FCSTD DOCUMENT  (FreeCAD 0.20R29603 (Git))
Label: wapama
License: All rights reserved
LicenseURL: http://en.wikipedia.org/wiki/All_rights_reserved
objects: Part::Vertex×236
note: 236 computed .brp shape members not serialized (recipe doc carries the construction recipe); baked Part::Feature solids carry a one-line shape summary decoded from their .brp

FEATURE [Part::Vertex] p1002  label="Sta-9_1/2-wl-13s"
  AttacherType = Attacher::AttachEngine3D
  X = 2498.72
  Y = 59966.3
  Z = 3962.4
FEATURE [Part::Vertex] p2002  label="Sta-9_1/2-wl-13p"
  AttacherType = Attacher::AttachEngine3D
  X = -2498.72
  Y = 59966.3
  Z = 3962.4
FEATURE [Part::Vertex] p1003  label="Sta-9_1/2-wl-11s"
  AttacherType = Attacher::AttachEngine3D
  X = 949.325
  Y = 59966.3
  Z = 3352.8
FEATURE [Part::Vertex] p2003  label="Sta-9_1/2-wl-11p"
  AttacherType = Attacher::AttachEngine3D
  X = -949.325
  Y = 59966.3
  Z = 3352.8
FEATURE [Part::Vertex] p1004  label="Sta-9_1/2-wl-9s"
  AttacherType = Attacher::AttachEngine3D
  X = 514.35
  Y = 59966.3
  Z = 2743.2
FEATURE [Part::Vertex] p2004  label="Sta-9_1/2-wl-9p"
  AttacherType = Attacher::AttachEngine3D
  X = -514.35
  Y = 59966.3
  Z = 2743.2
FEATURE [Part::Vertex] p1005  label="Sta-9_1/2-wl-7s"
  AttacherType = Attacher::AttachEngine3D
  X = 403.225
  Y = 59966.3
  Z = 2133.6
FEATURE [Part::Vertex] p2005  label="Sta-9_1/2-wl-7p"
  AttacherType = Attacher::AttachEngine3D
  X = -403.225
  Y = 59966.3
  Z = 2133.6
FEATURE [Part::Vertex] p1006  label="Sta-9_1/2-wl-5s"
  AttacherType = Attacher::AttachEngine3D
  X = 349.25
  Y = 59966.3
  Z = 1524
FEATURE [Part::Vertex] p2006  label="Sta-9_1/2-wl-5p"
  AttacherType = Attacher::AttachEngine3D
  X = -349.25
  Y = 59966.3
  Z = 1524
FEATURE [Part::Vertex] p1  label="Sta-9_1/2-wl-17s"
  AttacherType = Attacher::AttachEngine3D
  X = 5295.9
  Y = 59966.3
  Z = 5181.6
FEATURE [Part::Vertex] p2  label="Sta-9_1/2-wl-17p"
  AttacherType = Attacher::AttachEngine3D
  X = -5295.9
  Y = 59966.3
  Z = 5181.6
FEATURE [Part::Vertex] p1007  label="Sta-9_1/2-wl-15s"
  AttacherType = Attacher::AttachEngine3D
  X = 4229.1
  Y = 59966.3
  Z = 4572
FEATURE [Part::Vertex] p2007  label="Sta-9_1/2-wl-15p"
  AttacherType = Attacher::AttachEngine3D
  X = -4229.1
  Y = 59966.3
  Z = 4572
FEATURE [Part::Vertex] p1008  label="Sta-9_1/2-wl-3s"
  AttacherType = Attacher::AttachEngine3D
  X = 288.925
  Y = 59966.3
  Z = 914.4
FEATURE [Part::Vertex] p2008  label="Sta-9_1/2-wl-3p"
  AttacherType = Attacher::AttachEngine3D
  X = -288.925
  Y = 59966.3
  Z = 914.4
FEATURE [Part::Vertex] p1009  label="Sta-9_1/2-wl-1s"
  AttacherType = Attacher::AttachEngine3D
  X = 228.6
  Y = 59966.3
  Z = 304.8
FEATURE [Part::Vertex] p2009  label="Sta-9_1/2-wl-1p"
  AttacherType = Attacher::AttachEngine3D
  X = -228.6
  Y = 59966.3
  Z = 304.8
FEATURE [Part::Vertex] p1010  label="Sta-9-wl-17s"
  AttacherType = Attacher::AttachEngine3D
  X = 5813.43
  Y = 56811.7
  Z = 5181.6
FEATURE [Part::Vertex] p2010  label="Sta-9-wl-17p"
  AttacherType = Attacher::AttachEngine3D
  X = -5813.43
  Y = 56811.7
  Z = 5181.6
FEATURE [Part::Vertex] p1011  label="Sta-9-wl-15s"
  AttacherType = Attacher::AttachEngine3D
  X = 5594.35
  Y = 56811.7
  Z = 4572
FEATURE [Part::Vertex] p2011  label="Sta-9-wl-15p"
  AttacherType = Attacher::AttachEngine3D
  X = -5594.35
  Y = 56811.7
  Z = 4572
FEATURE [Part::Vertex] p1012  label="Sta-9-wl-13s"
  AttacherType = Attacher::AttachEngine3D
  X = 4908.55
  Y = 56811.7
  Z = 3962.4
FEATURE [Part::Vertex] p2012  label="Sta-9-wl-13p"
  AttacherType = Attacher::AttachEngine3D
  X = -4908.55
  Y = 56811.7
  Z = 3962.4
FEATURE [Part::Vertex] p1013  label="Sta-9-wl-11s"
  AttacherType = Attacher::AttachEngine3D
  X = 3698.88
  Y = 56811.7
  Z = 3352.8
FEATURE [Part::Vertex] p2013  label="Sta-9-wl-11p"
  AttacherType = Attacher::AttachEngine3D
  X = -3698.88
  Y = 56811.7
  Z = 3352.8
FEATURE [Part::Vertex] p1014  label="Sta-9-wl-9s"
  AttacherType = Attacher::AttachEngine3D
  X = 2362.2
  Y = 56811.7
  Z = 2743.2
FEATURE [Part::Vertex] p2014  label="Sta-9-wl-9p"
  AttacherType = Attacher::AttachEngine3D
  X = -2362.2
  Y = 56811.7
  Z = 2743.2
FEATURE [Part::Vertex] p1015  label="Sta-9-wl-7s"
  AttacherType = Attacher::AttachEngine3D
  X = 1317.63
  Y = 56811.7
  Z = 2133.6
FEATURE [Part::Vertex] p2015  label="Sta-9-wl-7p"
  AttacherType = Attacher::AttachEngine3D
  X = -1317.63
  Y = 56811.7
  Z = 2133.6
FEATURE [Part::Vertex] p1016  label="Sta-9-wl-5s"
  AttacherType = Attacher::AttachEngine3D
  X = 742.95
  Y = 56811.7
  Z = 1524
FEATURE [Part::Vertex] p2016  label="Sta-9-wl-5p"
  AttacherType = Attacher::AttachEngine3D
  X = -742.95
  Y = 56811.7
  Z = 1524
FEATURE [Part::Vertex] p1017  label="Sta-9-wl-3s"
  AttacherType = Attacher::AttachEngine3D
  X = 463.55
  Y = 56811.7
  Z = 914.4
FEATURE [Part::Vertex] p2017  label="Sta-9-wl-3p"
  AttacherType = Attacher::AttachEngine3D
  X = -463.55
  Y = 56811.7
  Z = 914.4
FEATURE [Part::Vertex] p1018  label="Sta-9-wl-1s"
  AttacherType = Attacher::AttachEngine3D
  X = 241.3
  Y = 56811.7
  Z = 304.8
FEATURE [Part::Vertex] p2018  label="Sta-9-wl-1p"
  AttacherType = Attacher::AttachEngine3D
  X = -241.3
  Y = 56811.7
  Z = 304.8
FEATURE [Part::Vertex] p1019  label="Sta-8-1/2-wl-17s"
  AttacherType = Attacher::AttachEngine3D
  X = 5978.52
  Y = 53655.5
  Z = 5181.6
FEATURE [Part::Vertex] p2019  label="Sta-8-1/2-wl-17p"
  AttacherType = Attacher::AttachEngine3D
  X = -5978.52
  Y = 53655.5
  Z = 5181.6
FEATURE [Part::Vertex] p1020  label="Sta-8-1/2-wl-15s"
  AttacherType = Attacher::AttachEngine3D
  X = 5937.25
  Y = 53655.5
  Z = 4572
FEATURE [Part::Vertex] p2020  label="Sta-8-1/2-wl-15p"
  AttacherType = Attacher::AttachEngine3D
  X = -5937.25
  Y = 53655.5
  Z = 4572
FEATURE [Part::Vertex] p1021  label="Sta-8-1/2-wl-13s"
  AttacherType = Attacher::AttachEngine3D
  X = 5715
  Y = 53655.5
  Z = 3962.4
FEATURE [Part::Vertex] p2021  label="Sta-8-1/2-wl-13p"
  AttacherType = Attacher::AttachEngine3D
  X = -5715
  Y = 53655.5
  Z = 3962.4
FEATURE [Part::Vertex] p1022  label="Sta-8-1/2-wl-11s"
  AttacherType = Attacher::AttachEngine3D
  X = 5200.65
  Y = 53655.5
  Z = 3352.8
FEATURE [Part::Vertex] p2022  label="Sta-8-1/2-wl-11p"
  AttacherType = Attacher::AttachEngine3D
  X = -5200.65
  Y = 53655.5
  Z = 3352.8
FEATURE [Part::Vertex] p1023  label="Sta-8-wl-17s"
  AttacherType = Attacher::AttachEngine3D
  X = 6045.2
  Y = 50499.3
  Z = 5181.6
FEATURE [Part::Vertex] p2023  label="Sta-8-wl-17p"
  AttacherType = Attacher::AttachEngine3D
  X = -6045.2
  Y = 50499.3
  Z = 5181.6
FEATURE [Part::Vertex] p1024  label="Sta-8-wl-15s"
  AttacherType = Attacher::AttachEngine3D
  X = 6038.85
  Y = 50499.3
  Z = 4572
FEATURE [Part::Vertex] p2024  label="Sta-8-wl-15p"
  AttacherType = Attacher::AttachEngine3D
  X = -6038.85
  Y = 50499.3
  Z = 4572
FEATURE [Part::Vertex] p1025  label="Sta-8-wl-13s"
  AttacherType = Attacher::AttachEngine3D
  X = 5953.12
  Y = 50499.3
  Z = 3962.4
FEATURE [Part::Vertex] p2025  label="Sta-8-wl-13p"
  AttacherType = Attacher::AttachEngine3D
  X = -5953.12
  Y = 50499.3
  Z = 3962.4
FEATURE [Part::Vertex] p1026  label="Sta-8-wl-11s"
  AttacherType = Attacher::AttachEngine3D
  X = 5737.23
  Y = 50499.3
  Z = 3352.8
FEATURE [Part::Vertex] p2026  label="Sta-8-wl-11p"
  AttacherType = Attacher::AttachEngine3D
  X = -5737.23
  Y = 50499.3
  Z = 3352.8
FEATURE [Part::Vertex] p1027  label="Sta-8-wl-9s"
  AttacherType = Attacher::AttachEngine3D
  X = 5245.1
  Y = 50499.3
  Z = 2743.2
FEATURE [Part::Vertex] p2027  label="Sta-8-wl-9p"
  AttacherType = Attacher::AttachEngine3D
  X = -5245.1
  Y = 50499.3
  Z = 2743.2
FEATURE [Part::Vertex] p1028  label="Sta-8-wl-7s"
  AttacherType = Attacher::AttachEngine3D
  X = 4254.5
  Y = 50499.3
  Z = 2133.6
FEATURE [Part::Vertex] p2028  label="Sta-8-wl-7p"
  AttacherType = Attacher::AttachEngine3D
  X = -4254.5
  Y = 50499.3
  Z = 2133.6
FEATURE [Part::Vertex] p1029  label="Sta-8-wl-5s"
  AttacherType = Attacher::AttachEngine3D
  X = 2857.5
  Y = 50499.3
  Z = 1524
FEATURE [Part::Vertex] p2029  label="Sta-8-wl-5p"
  AttacherType = Attacher::AttachEngine3D
  X = -2857.5
  Y = 50499.3
  Z = 1524
FEATURE [Part::Vertex] p1030  label="Sta-8-wl-3s"
  AttacherType = Attacher::AttachEngine3D
  X = 1463.67
  Y = 50499.3
  Z = 914.4
FEATURE [Part::Vertex] p2030  label="Sta-8-wl-3p"
  AttacherType = Attacher::AttachEngine3D
  X = -1463.67
  Y = 50499.3
  Z = 914.4
FEATURE [Part::Vertex] p1031  label="Sta-8-wl-1s"
  AttacherType = Attacher::AttachEngine3D
  X = 244.475
  Y = 50499.3
  Z = 304.8
FEATURE [Part::Vertex] p2031  label="Sta-8-wl-1p"
  AttacherType = Attacher::AttachEngine3D
  X = -244.475
  Y = 50499.3
  Z = 304.8
FEATURE [Part::Vertex] p1032  label="Sta-7-wl-17s"
  AttacherType = Attacher::AttachEngine3D
  X = 6149.97
  Y = 44186.9
  Z = 5181.6
FEATURE [Part::Vertex] p2032  label="Sta-7-wl-17p"
  AttacherType = Attacher::AttachEngine3D
  X = -6149.97
  Y = 44186.9
  Z = 5181.6
FEATURE [Part::Vertex] p1033  label="Sta-7-wl-15s"
  AttacherType = Attacher::AttachEngine3D
  X = 6162.68
  Y = 44186.9
  Z = 4572
FEATURE [Part::Vertex] p2033  label="Sta-7-wl-15p"
  AttacherType = Attacher::AttachEngine3D
  X = -6162.68
  Y = 44186.9
  Z = 4572
FEATURE [Part::Vertex] p1034  label="Sta-7-wl-13s"
  AttacherType = Attacher::AttachEngine3D
  X = 6146.8
  Y = 44186.9
  Z = 3962.4
FEATURE [Part::Vertex] p2034  label="Sta-7-wl-13p"
  AttacherType = Attacher::AttachEngine3D
  X = -6146.8
  Y = 44186.9
  Z = 3962.4
FEATURE [Part::Vertex] p1035  label="Sta-7-wl-11s"
  AttacherType = Attacher::AttachEngine3D
  X = 6092.82
  Y = 44186.9
  Z = 3352.8
FEATURE [Part::Vertex] p2035  label="Sta-7-wl-11p"
  AttacherType = Attacher::AttachEngine3D
  X = -6092.82
  Y = 44186.9
  Z = 3352.8
FEATURE [Part::Vertex] p1036  label="Sta-7-wl-9s"
  AttacherType = Attacher::AttachEngine3D
  X = 5940.43
  Y = 44186.9
  Z = 2743.2
FEATURE [Part::Vertex] p2036  label="Sta-7-wl-9p"
  AttacherType = Attacher::AttachEngine3D
  X = -5940.43
  Y = 44186.9
  Z = 2743.2
FEATURE [Part::Vertex] p1038  label="Sta-7-wl-5s"
  AttacherType = Attacher::AttachEngine3D
  X = 4695.82
  Y = 44186.9
  Z = 1524
FEATURE [Part::Vertex] p2038  label="Sta-7-wl-5p"
  AttacherType = Attacher::AttachEngine3D
  X = -4695.82
  Y = 44186.9
  Z = 1524
FEATURE [Part::Vertex] p1039  label="Sta-7-wl-7s"
  AttacherType = Attacher::AttachEngine3D
  X = 5584.83
  Y = 44186.9
  Z = 2133.6
FEATURE [Part::Vertex] p2039  label="Sta-7-wl-7p"
  AttacherType = Attacher::AttachEngine3D
  X = -5584.83
  Y = 44186.9
  Z = 2133.6
FEATURE [Part::Vertex] p1040  label="Sta-7-wl-3s"
  AttacherType = Attacher::AttachEngine3D
  X = 2755.9
  Y = 44186.9
  Z = 914.4
FEATURE [Part::Vertex] p2040  label="Sta-7-wl-3p"
  AttacherType = Attacher::AttachEngine3D
  X = -2755.9
  Y = 44186.9
  Z = 914.4
FEATURE [Part::Vertex] p1041  label="Sta-7-wl-1s"
  AttacherType = Attacher::AttachEngine3D
  X = 254
  Y = 44186.9
  Z = 304.8
FEATURE [Part::Vertex] p2041  label="Sta-7-wl-1p"
  AttacherType = Attacher::AttachEngine3D
  X = -254
  Y = 44186.9
  Z = 304.8
FEATURE [Part::Vertex] p1042  label="Sta-6-wl-15s"
  AttacherType = Attacher::AttachEngine3D
  X = 6191.25
  Y = 37874.4
  Z = 4572
FEATURE [Part::Vertex] p2042  label="Sta-6-wl-15p"
  AttacherType = Attacher::AttachEngine3D
  X = -6191.25
  Y = 37874.4
  Z = 4572
FEATURE [Part::Vertex] p1043  label="Sta-6-wl-17s"
  AttacherType = Attacher::AttachEngine3D
  X = 6172.2
  Y = 37874.4
  Z = 5181.6
FEATURE [Part::Vertex] p2043  label="Sta-6-wl-17p"
  AttacherType = Attacher::AttachEngine3D
  X = -6172.2
  Y = 37874.4
  Z = 5181.6
FEATURE [Part::Vertex] p1044  label="Sta-6-wl-13s"
  AttacherType = Attacher::AttachEngine3D
  X = 6210.3
  Y = 37874.4
  Z = 3962.4
FEATURE [Part::Vertex] p2044  label="Sta-6-wl-13p"
  AttacherType = Attacher::AttachEngine3D
  X = -6210.3
  Y = 37874.4
  Z = 3962.4
FEATURE [Part::Vertex] p1045  label="Sta-6-wl-11s"
  AttacherType = Attacher::AttachEngine3D
  X = 6184.9
  Y = 37874.4
  Z = 3352.8
FEATURE [Part::Vertex] p2045  label="Sta-6-wl-11p"
  AttacherType = Attacher::AttachEngine3D
  X = -6184.9
  Y = 37874.4
  Z = 3352.8
FEATURE [Part::Vertex] p1046  label="Sta-6-wl-9s"
  AttacherType = Attacher::AttachEngine3D
  X = 6080.13
  Y = 37874.4
  Z = 2743.2
FEATURE [Part::Vertex] p2046  label="Sta-6-wl-9p"
  AttacherType = Attacher::AttachEngine3D
  X = -6080.13
  Y = 37874.4
  Z = 2743.2
FEATURE [Part::Vertex] p1047  label="Sta-6-wl-7s"
  AttacherType = Attacher::AttachEngine3D
  X = 5807.07
  Y = 37874.4
  Z = 2133.6
FEATURE [Part::Vertex] p2047  label="Sta-6-wl-7p"
  AttacherType = Attacher::AttachEngine3D
  X = -5807.07
  Y = 37874.4
  Z = 2133.6
FEATURE [Part::Vertex] p1048  label="Sta-6-wl-5s"
  AttacherType = Attacher::AttachEngine3D
  X = 5102.22
  Y = 37874.4
  Z = 1524
FEATURE [Part::Vertex] p2048  label="Sta-6-wl-5p"
  AttacherType = Attacher::AttachEngine3D
  X = -5102.22
  Y = 37874.4
  Z = 1524
FEATURE [Part::Vertex] p1049  label="Sta-6-wl-3s"
  AttacherType = Attacher::AttachEngine3D
  X = 3127.38
  Y = 37874.4
  Z = 914.4
FEATURE [Part::Vertex] p2049  label="Sta-6-wl-3p"
  AttacherType = Attacher::AttachEngine3D
  X = -3127.38
  Y = 37874.4
  Z = 914.4
FEATURE [Part::Vertex] p1050  label="Sta-6-wl-1s"
  AttacherType = Attacher::AttachEngine3D
  X = 254
  Y = 37874.4
  Z = 304.8
FEATURE [Part::Vertex] p2050  label="Sta-6-wl-1p"
  AttacherType = Attacher::AttachEngine3D
  X = -254
  Y = 37874.4
  Z = 304.8
FEATURE [Part::Vertex] p1051  label="Sta-5-wl-17s"
  AttacherType = Attacher::AttachEngine3D
  X = 6181.73
  Y = 31562
  Z = 5181.6
FEATURE [Part::Vertex] p2051  label="Sta-5-wl-17p"
  AttacherType = Attacher::AttachEngine3D
  X = -6181.73
  Y = 31562
  Z = 5181.6
FEATURE [Part::Vertex] p1052  label="Sta-5-wl-15s"
  AttacherType = Attacher::AttachEngine3D
  X = 6203.95
  Y = 31562
  Z = 4572
FEATURE [Part::Vertex] p2052  label="Sta-5-wl-15p"
  AttacherType = Attacher::AttachEngine3D
  X = -6203.95
  Y = 31562
  Z = 4572
FEATURE [Part::Vertex] p1053  label="Sta-5-wl-13s"
  AttacherType = Attacher::AttachEngine3D
  X = 6213.48
  Y = 31562
  Z = 3962.4
FEATURE [Part::Vertex] p2053  label="Sta-5-wl-13p"
  AttacherType = Attacher::AttachEngine3D
  X = -6213.48
  Y = 31562
  Z = 3962.4
FEATURE [Part::Vertex] p1054  label="Sta-5-wl-11s"
  AttacherType = Attacher::AttachEngine3D
  X = 6200.78
  Y = 31562
  Z = 3352.8
FEATURE [Part::Vertex] p2054  label="Sta-5-wl-11p"
  AttacherType = Attacher::AttachEngine3D
  X = -6200.78
  Y = 31562
  Z = 3352.8
FEATURE [Part::Vertex] p1055  label="Sta-5-wl-9s"
  AttacherType = Attacher::AttachEngine3D
  X = 6099.18
  Y = 31562
  Z = 2743.2
FEATURE [Part::Vertex] p2055  label="Sta-5-wl-9p"
  AttacherType = Attacher::AttachEngine3D
  X = -6099.18
  Y = 31562
  Z = 2743.2
FEATURE [Part::Vertex] p1056  label="Sta-5-wl-7s"
  AttacherType = Attacher::AttachEngine3D
  X = 5873.75
  Y = 31562
  Z = 2133.6
FEATURE [Part::Vertex] p2056  label="Sta-5-wl-7p"
  AttacherType = Attacher::AttachEngine3D
  X = -5873.75
  Y = 31562
  Z = 2133.6
FEATURE [Part::Vertex] p1057  label="Sta-5-wl-5s"
  AttacherType = Attacher::AttachEngine3D
  X = 5213.35
  Y = 31562
  Z = 1524
FEATURE [Part::Vertex] p2057  label="Sta-5-wl-5p"
  AttacherType = Attacher::AttachEngine3D
  X = -5213.35
  Y = 31562
  Z = 1524
FEATURE [Part::Vertex] p1058  label="Sta-5-wl-3s"
  AttacherType = Attacher::AttachEngine3D
  X = 3251.2
  Y = 31562
  Z = 914.4
FEATURE [Part::Vertex] p2058  label="Sta-5-wl-3p"
  AttacherType = Attacher::AttachEngine3D
  X = -3251.2
  Y = 31562
  Z = 914.4
FEATURE [Part::Vertex] p1059  label="Sta-5-wl-1s"
  AttacherType = Attacher::AttachEngine3D
  X = 254
  Y = 31562
  Z = 304.8
FEATURE [Part::Vertex] p2059  label="Sta-5-wl-1p"
  AttacherType = Attacher::AttachEngine3D
  X = -254
  Y = 31562
  Z = 304.8
FEATURE [Part::Vertex] p1060  label="Sta-4-wl-17s"
  AttacherType = Attacher::AttachEngine3D
  X = 6210.3
  Y = 25249.6
  Z = 5181.6
FEATURE [Part::Vertex] p2060  label="Sta-4-wl-17p"
  AttacherType = Attacher::AttachEngine3D
  X = -6210.3
  Y = 25249.6
  Z = 5181.6
FEATURE [Part::Vertex] p1061  label="Sta-4-wl-15s"
  AttacherType = Attacher::AttachEngine3D
  X = 6242.05
  Y = 25249.6
  Z = 4572
FEATURE [Part::Vertex] p2061  label="Sta-4-wl-15p"
  AttacherType = Attacher::AttachEngine3D
  X = -6242.05
  Y = 25249.6
  Z = 4572
FEATURE [Part::Vertex] p1062  label="Sta-4-wl-13s"
  AttacherType = Attacher::AttachEngine3D
  X = 6248.4
  Y = 25249.6
  Z = 3962.4
FEATURE [Part::Vertex] p2062  label="Sta-4-wl-13p"
  AttacherType = Attacher::AttachEngine3D
  X = -6248.4
  Y = 25249.6
  Z = 3962.4
FEATURE [Part::Vertex] p1063  label="Sta-4-wl-11s"
  AttacherType = Attacher::AttachEngine3D
  X = 6223
  Y = 25249.6
  Z = 3352.8
FEATURE [Part::Vertex] p2063  label="Sta-4-wl-11p"
  AttacherType = Attacher::AttachEngine3D
  X = -6223
  Y = 25249.6
  Z = 3352.8
FEATURE [Part::Vertex] p1064  label="Sta-4-wl-9s"
  AttacherType = Attacher::AttachEngine3D
  X = 6143.62
  Y = 25249.6
  Z = 2743.2
FEATURE [Part::Vertex] p2064  label="Sta-4-wl-9p"
  AttacherType = Attacher::AttachEngine3D
  X = -6143.62
  Y = 25249.6
  Z = 2743.2
FEATURE [Part::Vertex] p1065  label="Sta-4-wl-7s"
  AttacherType = Attacher::AttachEngine3D
  X = 5911.85
  Y = 25249.6
  Z = 2133.6
FEATURE [Part::Vertex] p2065  label="Sta-4-wl-7p"
  AttacherType = Attacher::AttachEngine3D
  X = -5911.85
  Y = 25249.6
  Z = 2133.6
FEATURE [Part::Vertex] p1066  label="Sta-4-wl-5s"
  AttacherType = Attacher::AttachEngine3D
  X = 5299.08
  Y = 25249.6
  Z = 1524
FEATURE [Part::Vertex] p2066  label="Sta-4-wl-5p"
  AttacherType = Attacher::AttachEngine3D
  X = -5299.08
  Y = 25249.6
  Z = 1524
FEATURE [Part::Vertex] p1067  label="Sta-4-wl-3s"
  AttacherType = Attacher::AttachEngine3D
  X = 3251.2
  Y = 25249.6
  Z = 914.4
FEATURE [Part::Vertex] p2067  label="Sta-4-wl-3p"
  AttacherType = Attacher::AttachEngine3D
  X = -3251.2
  Y = 25249.6
  Z = 914.4
FEATURE [Part::Vertex] p1068  label="Sta-4-wl-1s"
  AttacherType = Attacher::AttachEngine3D
  X = 254
  Y = 25249.6
  Z = 304.8
FEATURE [Part::Vertex] p2068  label="Sta-4-wl-1p"
  AttacherType = Attacher::AttachEngine3D
  X = -254
  Y = 25249.6
  Z = 304.8
FEATURE [Part::Vertex] p1069  label="Sta-3-wl-17s"
  AttacherType = Attacher::AttachEngine3D
  X = 6191.25
  Y = 18937.2
  Z = 5181.6
FEATURE [Part::Vertex] p2069  label="Sta-3-wl-17p"
  AttacherType = Attacher::AttachEngine3D
  X = -6191.25
  Y = 18937.2
  Z = 5181.6
FEATURE [Part::Vertex] p1070  label="Sta-3-wl-15s"
  AttacherType = Attacher::AttachEngine3D
  X = 6207.12
  Y = 18937.2
  Z = 4572
FEATURE [Part::Vertex] p2070  label="Sta-3-wl-15p"
  AttacherType = Attacher::AttachEngine3D
  X = -6207.12
  Y = 18937.2
  Z = 4572
FEATURE [Part::Vertex] p1071  label="Sta-3-wl-13s"
  AttacherType = Attacher::AttachEngine3D
  X = 6203.95
  Y = 18937.2
  Z = 3962.4
FEATURE [Part::Vertex] p2071  label="Sta-3-wl-13p"
  AttacherType = Attacher::AttachEngine3D
  X = -6203.95
  Y = 18937.2
  Z = 3962.4
FEATURE [Part::Vertex] p1072  label="Sta-3-wl-11s"
  AttacherType = Attacher::AttachEngine3D
  X = 6175.38
  Y = 18937.2
  Z = 3352.8
FEATURE [Part::Vertex] p2072  label="Sta-3-wl-11p"
  AttacherType = Attacher::AttachEngine3D
  X = -6175.38
  Y = 18937.2
  Z = 3352.8
FEATURE [Part::Vertex] p1073  label="Sta-3-wl-9s"
  AttacherType = Attacher::AttachEngine3D
  X = 6051.55
  Y = 18937.2
  Z = 2743.2
FEATURE [Part::Vertex] p2073  label="Sta-3-wl-9p"
  AttacherType = Attacher::AttachEngine3D
  X = -6051.55
  Y = 18937.2
  Z = 2743.2
FEATURE [Part::Vertex] p1074  label="Sta-3-wl-7s"
  AttacherType = Attacher::AttachEngine3D
  X = 5740.4
  Y = 18937.2
  Z = 2133.6
FEATURE [Part::Vertex] p2074  label="Sta-3-wl-7p"
  AttacherType = Attacher::AttachEngine3D
  X = -5740.4
  Y = 18937.2
  Z = 2133.6
FEATURE [Part::Vertex] p1075  label="Sta-3-wl-5s"
  AttacherType = Attacher::AttachEngine3D
  X = 4997.45
  Y = 18937.2
  Z = 1524
FEATURE [Part::Vertex] p2075  label="Sta-3-wl-5p"
  AttacherType = Attacher::AttachEngine3D
  X = -4997.45
  Y = 18937.2
  Z = 1524
FEATURE [Part::Vertex] p1076  label="Sta-3-wl-3s"
  AttacherType = Attacher::AttachEngine3D
  X = 3060.7
  Y = 18937.2
  Z = 914.4
FEATURE [Part::Vertex] p2076  label="Sta-3-wl-3p"
  AttacherType = Attacher::AttachEngine3D
  X = -3060.7
  Y = 18937.2
  Z = 914.4
FEATURE [Part::Vertex] p1077  label="Sta-3-wl-1s"
  AttacherType = Attacher::AttachEngine3D
  X = 254
  Y = 18937.2
  Z = 304.8
FEATURE [Part::Vertex] p2077  label="Sta-3-wl-1p"
  AttacherType = Attacher::AttachEngine3D
  X = -254
  Y = 18937.2
  Z = 304.8
FEATURE [Part::Vertex] p1078  label="Sta-2-wl-17s"
  AttacherType = Attacher::AttachEngine3D
  X = 5813.43
  Y = 12624.8
  Z = 5181.6
FEATURE [Part::Vertex] p2078  label="Sta-2-wl-17p"
  AttacherType = Attacher::AttachEngine3D
  X = -5813.43
  Y = 12624.8
  Z = 5181.6
FEATURE [Part::Vertex] p1079  label="Sta-2-wl-15s"
  AttacherType = Attacher::AttachEngine3D
  X = 5794.38
  Y = 12624.8
  Z = 4572
FEATURE [Part::Vertex] p2079  label="Sta-2-wl-15p"
  AttacherType = Attacher::AttachEngine3D
  X = -5794.38
  Y = 12624.8
  Z = 4572
FEATURE [Part::Vertex] p1080  label="Sta-2-wl-13s"
  AttacherType = Attacher::AttachEngine3D
  X = 5734.05
  Y = 12624.8
  Z = 3962.4
FEATURE [Part::Vertex] p2080  label="Sta-2-wl-13p"
  AttacherType = Attacher::AttachEngine3D
  X = -5734.05
  Y = 12624.8
  Z = 3962.4
FEATURE [Part::Vertex] p1081  label="Sta-2-wl-11s"
  AttacherType = Attacher::AttachEngine3D
  X = 5597.52
  Y = 12624.8
  Z = 3352.8
FEATURE [Part::Vertex] p2081  label="Sta-2-wl-11p"
  AttacherType = Attacher::AttachEngine3D
  X = -5597.52
  Y = 12624.8
  Z = 3352.8
FEATURE [Part::Vertex] p1082  label="Sta-2-wl-9s"
  AttacherType = Attacher::AttachEngine3D
  X = 5311.77
  Y = 12624.8
  Z = 2743.2
FEATURE [Part::Vertex] p2082  label="Sta-2-wl-9p"
  AttacherType = Attacher::AttachEngine3D
  X = -5311.77
  Y = 12624.8
  Z = 2743.2
FEATURE [Part::Vertex] p1083  label="Sta-2-wl-7s"
  AttacherType = Attacher::AttachEngine3D
  X = 4794.25
  Y = 12624.8
  Z = 2133.6
FEATURE [Part::Vertex] p2083  label="Sta-2-wl-7p"
  AttacherType = Attacher::AttachEngine3D
  X = -4794.25
  Y = 12624.8
  Z = 2133.6
FEATURE [Part::Vertex] p1084  label="Sta-2-wl-5s"
  AttacherType = Attacher::AttachEngine3D
  X = 3879.85
  Y = 12624.8
  Z = 1524
FEATURE [Part::Vertex] p2084  label="Sta-2-wl-5p"
  AttacherType = Attacher::AttachEngine3D
  X = -3879.85
  Y = 12624.8
  Z = 1524
FEATURE [Part::Vertex] p1085  label="Sta-2-wl-3s"
  AttacherType = Attacher::AttachEngine3D
  X = 2333.62
  Y = 12624.8
  Z = 914.4
FEATURE [Part::Vertex] p2085  label="Sta-2-wl-3p"
  AttacherType = Attacher::AttachEngine3D
  X = -2333.62
  Y = 12624.8
  Z = 914.4
FEATURE [Part::Vertex] p1086  label="Sta-2-wl-1s"
  AttacherType = Attacher::AttachEngine3D
  X = 254
  Y = 12624.8
  Z = 304.8
FEATURE [Part::Vertex] p2086  label="Sta-2-wl-1p"
  AttacherType = Attacher::AttachEngine3D
  X = -254
  Y = 12624.8
  Z = 304.8
FEATURE [Part::Vertex] p1087  label="Sta-1-1/2-wl-17s"
  AttacherType = Attacher::AttachEngine3D
  X = 5203.83
  Y = 9468.61
  Z = 5181.6
FEATURE [Part::Vertex] p2087  label="Sta-1-1/2-wl-17p"
  AttacherType = Attacher::AttachEngine3D
  X = -5203.83
  Y = 9468.61
  Z = 5181.6
FEATURE [Part::Vertex] p1088  label="Sta-1-1/2-wl-15s"
  AttacherType = Attacher::AttachEngine3D
  X = 5130.8
  Y = 9468.61
  Z = 4572
FEATURE [Part::Vertex] p2088  label="Sta-1-1/2-wl-15p"
  AttacherType = Attacher::AttachEngine3D
  X = -5130.8
  Y = 9468.61
  Z = 4572
FEATURE [Part::Vertex] p1089  label="Sta-1-1/2-wl-13s"
  AttacherType = Attacher::AttachEngine3D
  X = 4997.45
  Y = 9468.61
  Z = 3962.4
FEATURE [Part::Vertex] p2089  label="Sta-1-1/2-wl-13p"
  AttacherType = Attacher::AttachEngine3D
  X = -4997.45
  Y = 9468.61
  Z = 3962.4
FEATURE [Part::Vertex] p1090  label="Sta-1-1/2-wl-11s"
  AttacherType = Attacher::AttachEngine3D
  X = 4772.03
  Y = 9468.61
  Z = 3352.8
FEATURE [Part::Vertex] p2090  label="Sta-1-1/2-wl-11p"
  AttacherType = Attacher::AttachEngine3D
  X = -4772.03
  Y = 9468.61
  Z = 3352.8
FEATURE [Part::Vertex] p1091  label="Sta-1-1/2-wl-9s"
  AttacherType = Attacher::AttachEngine3D
  X = 4406.9
  Y = 9468.61
  Z = 2743.2
FEATURE [Part::Vertex] p2091  label="Sta-1-1/2-wl-9p"
  AttacherType = Attacher::AttachEngine3D
  X = -4406.9
  Y = 9468.61
  Z = 2743.2
FEATURE [Part::Vertex] p1092  label="Sta-1-1/2-wl-7s"
  AttacherType = Attacher::AttachEngine3D
  X = 3848.1
  Y = 9468.61
  Z = 2133.6
FEATURE [Part::Vertex] p2092  label="Sta-1-1/2-wl-7p"
  AttacherType = Attacher::AttachEngine3D
  X = -3848.1
  Y = 9468.61
  Z = 2133.6
FEATURE [Part::Vertex] p1093  label="Sta-1-1/2-wl-5s"
  AttacherType = Attacher::AttachEngine3D
  X = 2997.2
  Y = 9468.61
  Z = 1524
FEATURE [Part::Vertex] p2093  label="Sta-1-1/2-wl-5p"
  AttacherType = Attacher::AttachEngine3D
  X = -2997.2
  Y = 9468.61
  Z = 1524
FEATURE [Part::Vertex] p1094  label="Sta-1-1/2-wl-3s"
  AttacherType = Attacher::AttachEngine3D
  X = 1762.12
  Y = 9468.61
  Z = 914.4
FEATURE [Part::Vertex] p2094  label="Sta-1-1/2-wl-3p"
  AttacherType = Attacher::AttachEngine3D
  X = -1762.12
  Y = 9468.61
  Z = 914.4
FEATURE [Part::Vertex] p1095  label="Sta-1-1/2-wl-1s"
  AttacherType = Attacher::AttachEngine3D
  X = 254
  Y = 9468.61
  Z = 304.8
FEATURE [Part::Vertex] p2095  label="Sta-1-1/2-wl-1p"
  AttacherType = Attacher::AttachEngine3D
  X = -254
  Y = 9468.61
  Z = 304.8
FEATURE [Part::Vertex] p1096  label="Sta-1-wl-17s"
  AttacherType = Attacher::AttachEngine3D
  X = 4089.4
  Y = 6312.41
  Z = 5181.6
FEATURE [Part::Vertex] p2096  label="Sta-1-wl-17p"
  AttacherType = Attacher::AttachEngine3D
  X = -4089.4
  Y = 6312.41
  Z = 5181.6
FEATURE [Part::Vertex] p1097  label="Sta-1-wl-15s"
  AttacherType = Attacher::AttachEngine3D
  X = 3959.23
  Y = 6312.41
  Z = 4572
FEATURE [Part::Vertex] p2097  label="Sta-1-wl-15p"
  AttacherType = Attacher::AttachEngine3D
  X = -3959.23
  Y = 6312.41
  Z = 4572
FEATURE [Part::Vertex] p1098  label="Sta-1-wl-13s"
  AttacherType = Attacher::AttachEngine3D
  X = 3762.38
  Y = 6312.41
  Z = 3962.4
FEATURE [Part::Vertex] p2098  label="Sta-1-wl-13p"
  AttacherType = Attacher::AttachEngine3D
  X = -3762.38
  Y = 6312.41
  Z = 3962.4
FEATURE [Part::Vertex] p1099  label="Sta-1-wl-11s"
  AttacherType = Attacher::AttachEngine3D
  X = 3492.5
  Y = 6312.41
  Z = 3352.8
FEATURE [Part::Vertex] p2099  label="Sta-1-wl-11p"
  AttacherType = Attacher::AttachEngine3D
  X = -3492.5
  Y = 6312.41
  Z = 3352.8
FEATURE [Part::Vertex] p1100  label="Sta-1-wl-9s"
  AttacherType = Attacher::AttachEngine3D
  X = 3117.85
  Y = 6312.41
  Z = 2743.2
FEATURE [Part::Vertex] p2100  label="Sta-1-wl-9p"
  AttacherType = Attacher::AttachEngine3D
  X = -3117.85
  Y = 6312.41
  Z = 2743.2
FEATURE [Part::Vertex] p1101  label="Sta-1-wl-7s"
  AttacherType = Attacher::AttachEngine3D
  X = 2600.33
  Y = 6312.41
  Z = 2133.6
FEATURE [Part::Vertex] p2101  label="Sta-1-wl-7p"
  AttacherType = Attacher::AttachEngine3D
  X = -2600.33
  Y = 6312.41
  Z = 2133.6
FEATURE [Part::Vertex] p1102  label="Sta-1-wl-5s"
  AttacherType = Attacher::AttachEngine3D
  X = 1930.4
  Y = 6312.41
  Z = 1524
FEATURE [Part::Vertex] p2102  label="Sta-1-wl-5p"
  AttacherType = Attacher::AttachEngine3D
  X = -1930.4
  Y = 6312.41
  Z = 1524
FEATURE [Part::Vertex] p1103  label="Sta-1-wl-3s"
  AttacherType = Attacher::AttachEngine3D
  X = 1095.38
  Y = 6312.41
  Z = 914.4
FEATURE [Part::Vertex] p2103  label="Sta-1-wl-3p"
  AttacherType = Attacher::AttachEngine3D
  X = -1095.38
  Y = 6312.41
  Z = 914.4
FEATURE [Part::Vertex] p1104  label="Sta-1-wl-1s"
  AttacherType = Attacher::AttachEngine3D
  X = 241.3
  Y = 6312.41
  Z = 304.8
FEATURE [Part::Vertex] p2104  label="Sta-1-wl-1p"
  AttacherType = Attacher::AttachEngine3D
  X = -241.3
  Y = 6312.41
  Z = 304.8
FEATURE [Part::Vertex] p1105  label="Sta-8-1/2-wl-9s"
  AttacherType = Attacher::AttachEngine3D
  X = 4156.07
  Y = 53655.5
  Z = 2743.2
FEATURE [Part::Vertex] p2105  label="Sta-8-1/2-wl-9p"
  AttacherType = Attacher::AttachEngine3D
  X = -4156.07
  Y = 53655.5
  Z = 2743.2
FEATURE [Part::Vertex] p1106  label="Sta-8-1/2-wl-7s"
  AttacherType = Attacher::AttachEngine3D
  X = 2895.6
  Y = 53655.5
  Z = 2133.6
FEATURE [Part::Vertex] p2106  label="Sta-8-1/2-wl-7p"
  AttacherType = Attacher::AttachEngine3D
  X = -2895.6
  Y = 53655.5
  Z = 2133.6
FEATURE [Part::Vertex] p1107  label="Sta-8-1/2-wl-5s"
  AttacherType = Attacher::AttachEngine3D
  X = 1752.6
  Y = 53655.5
  Z = 1524
FEATURE [Part::Vertex] p2107  label="Sta-8-1/2-wl-5p"
  AttacherType = Attacher::AttachEngine3D
  X = -1752.6
  Y = 53655.5
  Z = 1524
FEATURE [Part::Vertex] p1108  label="Sta-8-1/2-wl-3s"
  AttacherType = Attacher::AttachEngine3D
  X = 923.925
  Y = 53655.5
  Z = 914.4
FEATURE [Part::Vertex] p2108  label="Sta-8-1/2-wl-3p"
  AttacherType = Attacher::AttachEngine3D
  X = -923.925
  Y = 53655.5
  Z = 914.4
FEATURE [Part::Vertex] p1109  label="Sta-8-1/2-wl-1s"
  AttacherType = Attacher::AttachEngine3D
  X = 250.825
  Y = 53655.5
  Z = 304.8
FEATURE [Part::Vertex] p2109  label="Sta-8-1/2-wl-1p"
  AttacherType = Attacher::AttachEngine3D
  X = -250.825
  Y = 53655.5
  Z = 304.8
FEATURE [Part::Vertex] p1110  label="Sta-0-wl-17s"
  AttacherType = Attacher::AttachEngine3D
  X = 2301.88
  Y = 3156.2
  Z = 5181.6
FEATURE [Part::Vertex] p2110  label="Sta-0-wl-17p"
  AttacherType = Attacher::AttachEngine3D
  X = -2301.88
  Y = 3156.2
  Z = 5181.6
FEATURE [Part::Vertex] p1111  label="Sta-0-wl-15s"
  AttacherType = Attacher::AttachEngine3D
  X = 2184.4
  Y = 3156.2
  Z = 4572
FEATURE [Part::Vertex] p2111  label="Sta-0-wl-15p"
  AttacherType = Attacher::AttachEngine3D
  X = -2184.4
  Y = 3156.2
  Z = 4572
FEATURE [Part::Vertex] p1112  label="Sta-0-wl-13s"
  AttacherType = Attacher::AttachEngine3D
  X = 2022.48
  Y = 3156.2
  Z = 3962.4
FEATURE [Part::Vertex] p2112  label="Sta-0-wl-13p"
  AttacherType = Attacher::AttachEngine3D
  X = -2022.48
  Y = 3156.2
  Z = 3962.4
FEATURE [Part::Vertex] p1113  label="Sta-0-wl-11s"
  AttacherType = Attacher::AttachEngine3D
  X = 1800.23
  Y = 3156.2
  Z = 3352.8
FEATURE [Part::Vertex] p2113  label="Sta-0-wl-11p"
  AttacherType = Attacher::AttachEngine3D
  X = -1800.23
  Y = 3156.2
  Z = 3352.8
FEATURE [Part::Vertex] p1114  label="Sta-0-wl-9s"
  AttacherType = Attacher::AttachEngine3D
  X = 1520.83
  Y = 3156.2
  Z = 2743.2
FEATURE [Part::Vertex] p2114  label="Sta-0-wl-9p"
  AttacherType = Attacher::AttachEngine3D
  X = -1520.83
  Y = 3156.2
  Z = 2743.2
FEATURE [Part::Vertex] p1115  label="Sta-0-wl-7s"
  AttacherType = Attacher::AttachEngine3D
  X = 1168.4
  Y = 3156.2
  Z = 2133.6
FEATURE [Part::Vertex] p2115  label="Sta-0-wl-7p"
  AttacherType = Attacher::AttachEngine3D
  X = -1168.4
  Y = 3156.2
  Z = 2133.6
FEATURE [Part::Vertex] p1116  label="Sta-0-wl-5s"
  AttacherType = Attacher::AttachEngine3D
  X = 809.625
  Y = 3156.2
  Z = 1524
FEATURE [Part::Vertex] p2116  label="Sta-0-wl-5p"
  AttacherType = Attacher::AttachEngine3D
  X = -809.625
  Y = 3156.2
  Z = 1524
FEATURE [Part::Vertex] p1117  label="Sta-0-wl-3s"
  AttacherType = Attacher::AttachEngine3D
  X = 492.125
  Y = 3156.2
  Z = 914.4
FEATURE [Part::Vertex] p2117  label="Sta-0-wl-3p"
  AttacherType = Attacher::AttachEngine3D
  X = -492.125
  Y = 3156.2
  Z = 914.4
FEATURE [Part::Vertex] p1118  label="Sta-0-wl-1s"
  AttacherType = Attacher::AttachEngine3D
  X = 215.9
  Y = 3156.2
  Z = 304.8
FEATURE [Part::Vertex] p2118  label="Sta-0-wl-1p"
  AttacherType = Attacher::AttachEngine3D
  X = -215.9
  Y = 3156.2
  Z = 304.8
FEATURE [Part::Vertex] p1119  label="Sta-0-wl-17s001"
  AttacherType = Attacher::AttachEngine3D
  X = 190.5
  Y = 0
  Z = 5181.6
FEATURE [Part::Vertex] p2119  label="Sta-0-wl-17p001"
  AttacherType = Attacher::AttachEngine3D
  X = -190.5
  Y = 0
  Z = 5181.6
